# Revit family: O14111001_Lavamanos Milano de Colgar Blanco
name_source: partatom
category: Plumbing Fixtures
units: mm (PartAtom-declared; Revit-internal decimal feet)

## family parameters
Always vertical = Yes
Cut with Voids When Loaded = No
OmniClass Number = 23.31.13.11
OmniClass Title = Single Sinks
Part Type = Normal
Room Calculation Point = No
Round Connector Dimension = Use Diameter
Shared = No
Work Plane-Based = No

## types (8) — shared parameters
Acabado = Brillante
Alto = 19.3 cm
Ancho = 53.5 cm
Colección = 200102
Creado por = IDD
Description = Para los espacios más contemporáneo el lavamanos Milano de colgar será perfecto para tu baño. ¡Cómpralo ahora!
Dimensión del pozo = 48.50 cm
Diámetro del desagüe = 41 mm
Fecha de creación = 5/08/2020
Forma = Ovalado
Garantía = Garantia completa para siempre en la porcelana
Incluye = Lavamanos de colgar
Largo = 39 cm
Línea = Milano
Materiales = Porcelana sanitaria
No incluye = No incluye grifería
Productos compatibles = Grifería sencilla, Grifería monocontrol baja y media, Grifería 4 Pulgadas
Profundidad del pozo = 18 cm
Tipo de desagüe = Expuesto
Tipo de instalación = A pared
Tipo de lavamanos = De colgar
URL = https://corona.co
Uso = Residencial

## per-type parameters (varying)
| type | Material | Pedestal |
| Blanco | Corona_Porcelana_Sanitaria_Blanco | Yes |
| Hueso | Corona_Porcelana_Sanitaria_Hueso | Yes |
| Azul_claro | Corona_Porcelana_Sanitaria_Azul_Claro | Yes |
| Azul | Corona_Porcelana_Sanitaria_Azul | Yes |
| Azul_oscuro | Corona_Porcelana_Sanitaria_Azul_Oscuro | No |
| Verde_claro | Corona_Porcelana_Sanitaria_Verde_Claro | No |
| Verde_oscuro | Corona_Porcelana_Sanitaria_Verde_Oscuro) | Yes |
| Negro | Corona_Porcelana_Sanitaria_Negro | No |

## geometry (parser evidence)
native form markers: Sweep x4
no freeform markers — native parametric forms only
